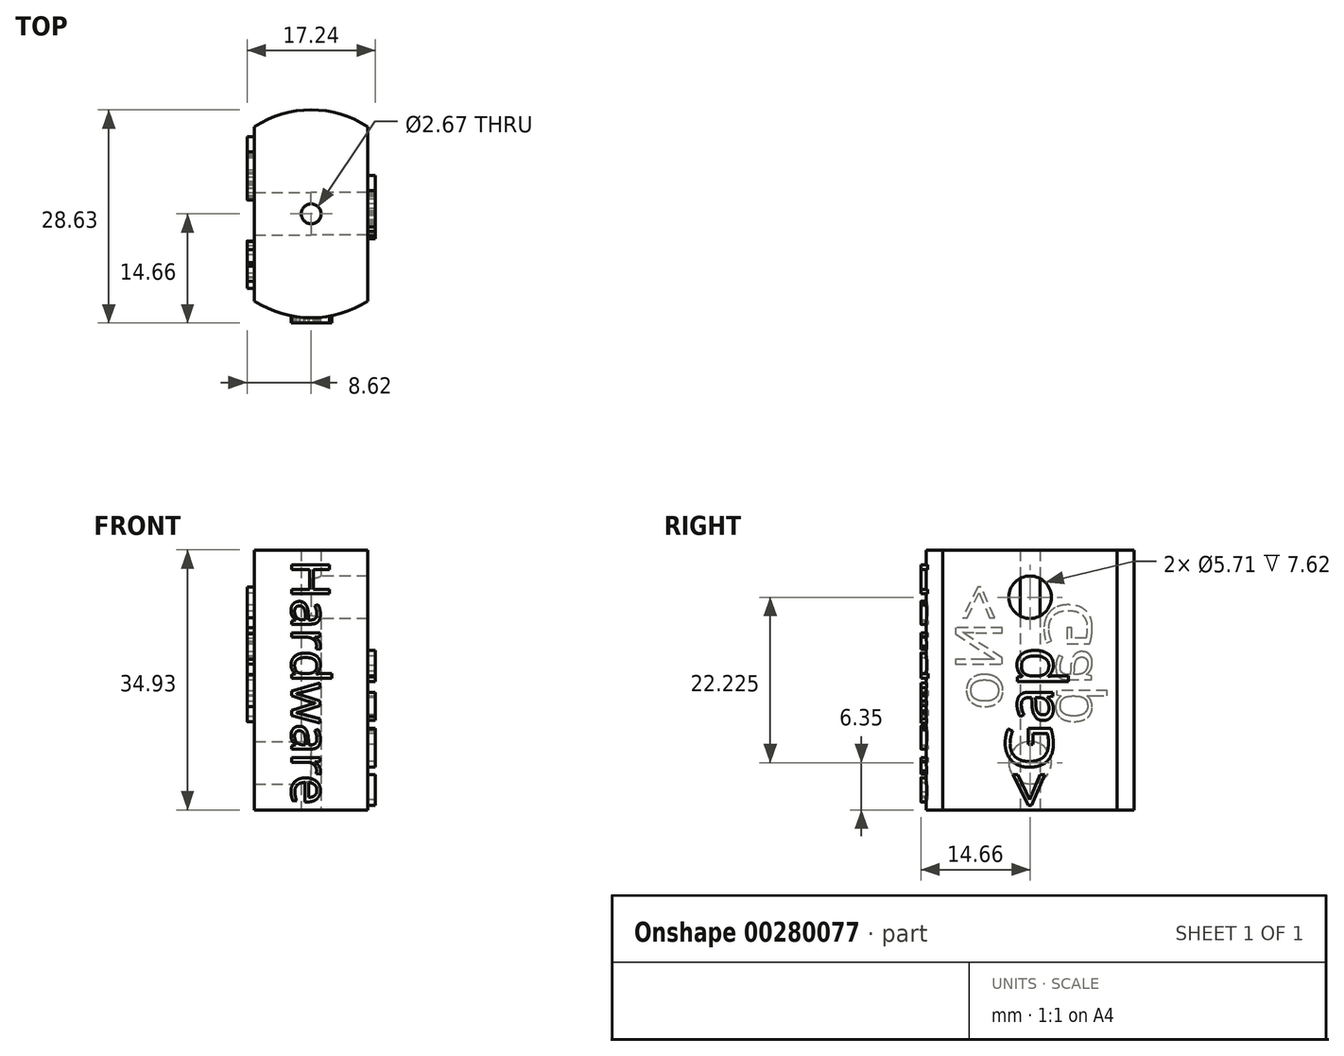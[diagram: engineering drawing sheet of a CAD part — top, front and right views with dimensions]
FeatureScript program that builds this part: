
annotation { "Feature Type Name" : "Feature", "Feature Type Description" : "" }
export const myFeature = defineFeature(function(context is Context, id is Id, definition is map)
    precondition{}
    {
        {
            var Q0;
            Q0=qCreatedBy(makeId("Top.planeOp"),FACE);
            var sketch = newSketch(context, id + "F0", { "sketchPlane" : qUnion([Q0])});
            skArc(sketch, "E0", {"start": v(-7.62, -11.7) * mm, "mid": v(0, -13.97) * mm, "end": v(7.62, -11.7) * mm});
            skCircle(sketch, "E1", {"center": v(0, 0) * mm, "radius": 1.33 * mm});
            skLineSegment(sketch, "E2", {"start": v(-7.62, -11.7) * mm, "end": v(-7.62, 11.7) * mm});
            skLineSegment(sketch, "E3.MirrorCS", {"start": v(7.62, -11.7) * mm, "end": v(7.62, 11.7) * mm});
            skArc(sketch, "E4.trimOffspring", {"start": v(7.62, 11.7) * mm, "mid": v(0, 13.97) * mm, "end": v(-7.62, 11.7) * mm});
            skSolve(sketch);
        }
        {
            var Q0;
            Q0=qSketchRegion(id+"F0",true);
            extrude(context, id + "F1", {"entities" : qUnion([Q0]), "depth" : 34.92 * mm});
        }
        {
            var Q0;
            Q0=qCreatedBy(makeId("Right.planeOp"),FACE);
            var sketch = newSketch(context, id + "F2", { "sketchPlane" : qUnion([Q0])});
            skCircle(sketch, "E5", {"center": v(0, 28.58) * mm, "radius": 2.86 * mm});
            skSolve(sketch);
        }
        {
            var Q0;
            Q0=qSketchRegion(id+"F2",true);
            var Q1;
            Q1=makeQuery(id+"F1.opExtrude","SWEPT_FACE",FACE,{"disambiguationData":[OSD([sQuery(id+"F0.wireOp",EDGE,"E3.MirrorCS")])]});
            extrude(context, id + "F3", {"entities" : qUnion([Q0]), "operationType" : NewBodyOperationType.REMOVE, "endBound" : BoundingType.UP_TO_SURFACE, "endBoundEntityFace" : qUnion([Q1]), "depth" : 6.35 * mm});
        }
        {
            var Q0;
            Q0=qCreatedBy(makeId("Right.planeOp"),FACE);
            var sketch = newSketch(context, id + "F4", { "sketchPlane" : qUnion([Q0])});
            skCircle(sketch, "E6", {"center": v(0, 6.35) * mm, "radius": 2.86 * mm});
            skSolve(sketch);
        }
        {
            var Q0;
            Q0=qSketchRegion(id+"F4",true);
            var Q1;
            Q1=makeQuery(id+"F1.opExtrude","SWEPT_FACE",FACE,{"disambiguationData":[OSD([sQuery(id+"F0.wireOp",EDGE,"E2")])]});
            extrude(context, id + "F5", {"entities" : qUnion([Q0]), "operationType" : NewBodyOperationType.REMOVE, "endBound" : BoundingType.UP_TO_SURFACE, "oppositeDirection" : true, "endBoundEntityFace" : qUnion([Q1]), "depth" : 25.4 * mm});
        }
        {
            var Q0;
            Q0=makeQuery(id+"F1.opExtrude","SWEPT_FACE",FACE,{"disambiguationData":[OSD([sQuery(id+"F0.wireOp",EDGE,"E2")])]});
            var sketch = newSketch(context, id + "F6", { "sketchPlane" : qUnion([Q0])});
            skText(sketch, "E7", { "text": " <No\n  Gap", "fontName": "OpenSans-Regular.ttf"});
            const initialGuessF6  = {"E7": [0.00374, 0.03269, 0, -1, 0.00635]};
            skSetInitialGuess(sketch, initialGuessF6);
            skSolve(sketch);
        }
        {
            var Q0;
            Q0=qSketchRegion(id+"F6",true);
            extrude(context, id + "F7", {"entities" : qUnion([Q0]), "operationType" : NewBodyOperationType.ADD, "depth" : 1 * mm});
        }
        {
            var Q0;
            Q0=makeQuery(id+"F1.opExtrude","SWEPT_FACE",FACE,{"disambiguationData":[OSD([sQuery(id+"F0.wireOp",EDGE,"E3.MirrorCS")])]});
            var sketch = newSketch(context, id + "F8", { "sketchPlane" : qUnion([Q0])});
            skText(sketch, "E8", { "text": "<Gap", "fontName": "OpenSans-Regular.ttf"});
            const initialGuessF8  = {"E8": [0.00304, 0.00015, 0, 1, 0.00635]};
            skSetInitialGuess(sketch, initialGuessF8);
            skSolve(sketch);
        }
        {
            var Q0;
            Q0=qSketchRegion(id+"F8",true);
            extrude(context, id + "F9", {"entities" : qUnion([Q0]), "operationType" : NewBodyOperationType.ADD, "depth" : 1 * mm});
        }
        {
            var Q0;
            Q0=qCreatedBy(makeId("Front.planeOp"),FACE);
            cPlane(context, id + "F10", {"entities" : qUnion([Q0]), "cplaneType" : CPlaneType.OFFSET, "offset" : 10.16 * mm, "width" : 152.4 * mm, "height" : 152.4 * mm});
        }
        {
            var Q0;
            Q0=qCreatedBy(id+"F10.planeOp",FACE);
            var sketch = newSketch(context, id + "F11", { "sketchPlane" : qUnion([Q0])});
            skText(sketch, "E9", { "text": "Hardware", "fontName": "OpenSans-Regular.ttf"});
            const initialGuessF11  = {"E9": [-0.00263, 0.0336, 0, -1, 0.00513]};
            skSetInitialGuess(sketch, initialGuessF11);
            skSolve(sketch);
        }
        {
            var Q0;
            Q0=qSketchRegion(id+"F11",true);
            extrude(context, id + "F12", {"entities" : qUnion([Q0]), "operationType" : NewBodyOperationType.ADD, "depth" : 4.5 * mm});
        }
    });
